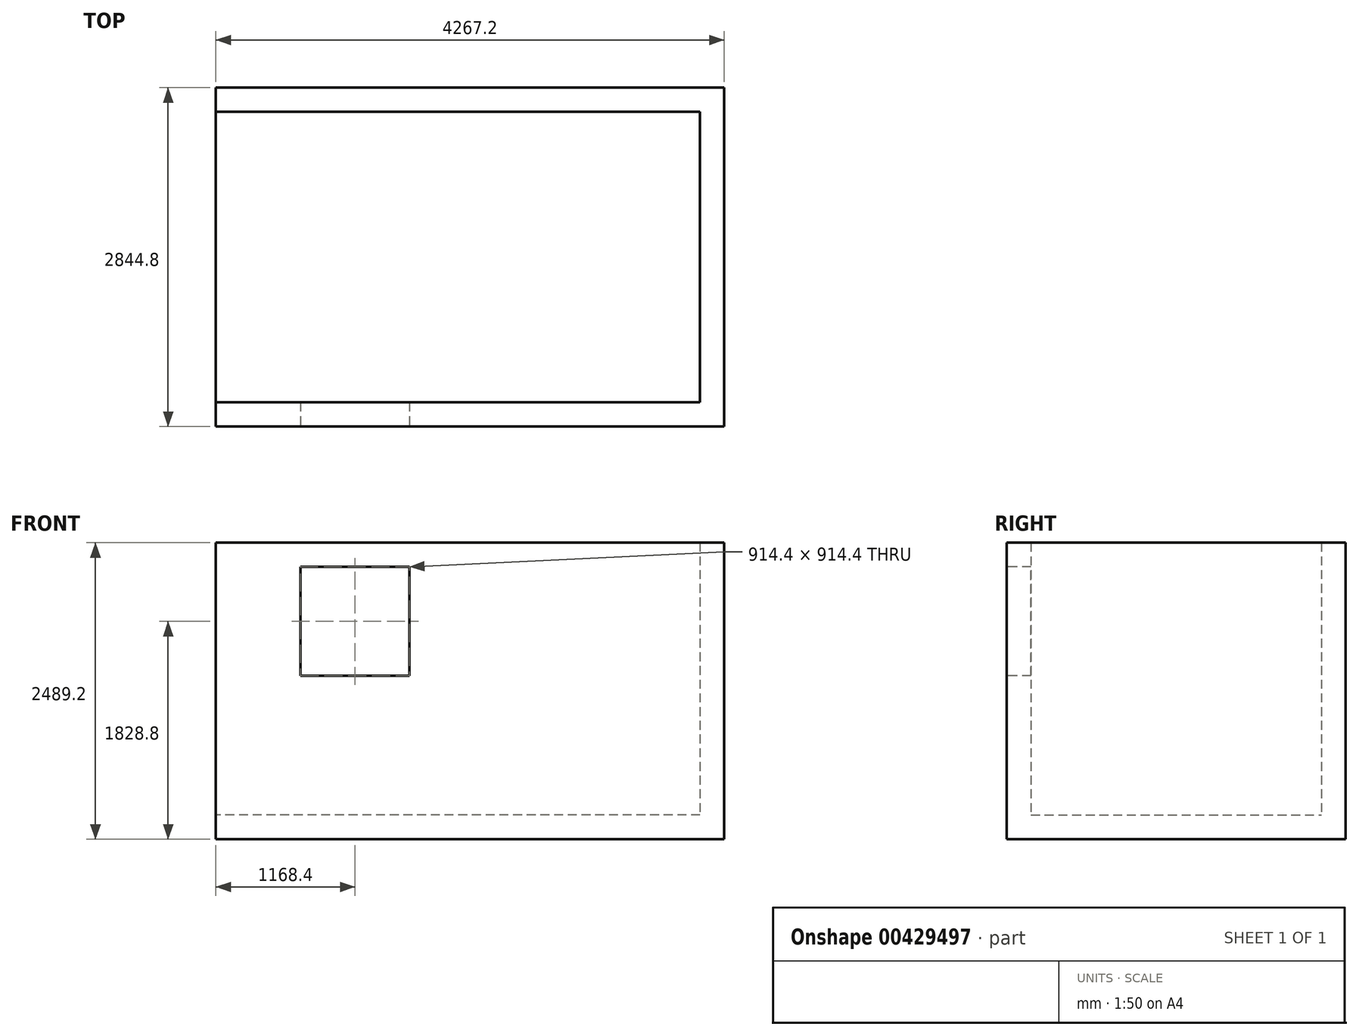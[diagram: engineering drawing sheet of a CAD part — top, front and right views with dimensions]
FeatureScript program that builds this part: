
annotation { "Feature Type Name" : "Feature", "Feature Type Description" : "" }
export const myFeature = defineFeature(function(context is Context, id is Id, definition is map)
    precondition{}
    {
        {
            var Q0;
            Q0=qCreatedBy(makeId("Top.planeOp"),FACE);
            var sketch = newSketch(context, id + "F0", { "sketchPlane" : qUnion([Q0])});
            skLineSegment(sketch, "E0.bottom", {"start": v(0, 0) * mm, "end": v(4267.2, 0) * mm});
            skLineSegment(sketch, "E0.top", {"start": v(0, 2844.8) * mm, "end": v(4267.2, 2844.8) * mm});
            skLineSegment(sketch, "E0.left", {"start": v(0, 0) * mm, "end": v(0, 2844.8) * mm});
            skLineSegment(sketch, "E0.right", {"start": v(4267.2, 0) * mm, "end": v(4267.2, 2844.8) * mm});
            skSolve(sketch);
        }
        {
            var Q0;
            Q0 = qSketchRegion(id + "F0", true);
            extrude(context, id + "F1", {"entities" : qUnion([Q0]), "depth" : 203.2 * mm});
        }
        {
            var Q0;
            Q0=makeQuery(id+"F1.opExtrude","CAP_FACE",FACE,{"disambiguationData":[OSD([sQuery(id+"F0.wireOp",EDGE,"E0.bottom"),sQuery(id+"F0.wireOp",EDGE,"E0.top"),sQuery(id+"F0.wireOp",EDGE,"E0.left"),sQuery(id+"F0.wireOp",EDGE,"E0.right")])],"isStart":false});
            var sketch = newSketch(context, id + "F2", { "sketchPlane" : qUnion([Q0])});
            skLineSegment(sketch, "E1.0", {"start": v(0, 0) * mm, "end": v(4267.2, 0) * mm});
            skLineSegment(sketch, "E1.1", {"start": v(4267.2, 0) * mm, "end": v(4267.2, 2844.8) * mm});
            skLineSegment(sketch, "E1.2", {"start": v(0, 2844.8) * mm, "end": v(4267.2, 2844.8) * mm});
            skLineSegment(sketch, "E2", {"start": v(0, 2844.8) * mm, "end": v(0, 2641.6) * mm});
            skLineSegment(sketch, "E3", {"start": v(0, 2641.6) * mm, "end": v(4064, 2641.6) * mm});
            skLineSegment(sketch, "E4", {"start": v(4064, 2641.6) * mm, "end": v(4064, 203.2) * mm});
            skLineSegment(sketch, "E5", {"start": v(4064, 203.2) * mm, "end": v(0, 203.2) * mm});
            skLineSegment(sketch, "E6", {"start": v(0, 203.2) * mm, "end": v(0, 0) * mm});
            skSolve(sketch);
        }
        {
            var Q0;
            Q0 = qSketchRegion(id + "F2", true);
            extrude(context, id + "F3", {"entities" : qUnion([Q0]), "operationType" : NewBodyOperationType.ADD, "depth" : 2286 * mm});
        }
        {
            var Q0;
            Q0=makeQuery(id+"F3.boolean.opBoolean","MERGE",FACE,{"derivedFrom":[makeQuery(id+"F1.opExtrude","SWEPT_FACE",FACE,{"disambiguationData":[OSD([sQuery(id+"F0.wireOp",EDGE,"E0.bottom")])]}),makeQuery(id+"F3.opExtrude","SWEPT_FACE",FACE,{"disambiguationData":[OSD([sQuery(id+"F2.wireOp",EDGE,"E1.0")])]})]});
            var sketch = newSketch(context, id + "F4", { "sketchPlane" : qUnion([Q0])});
            skLineSegment(sketch, "E7.bottom", {"start": v(711.2, 2286) * mm, "end": v(1625.6, 2286) * mm});
            skLineSegment(sketch, "E7.top", {"start": v(711.2, 1371.6) * mm, "end": v(1625.6, 1371.6) * mm});
            skLineSegment(sketch, "E7.left", {"start": v(711.2, 2286) * mm, "end": v(711.2, 1371.6) * mm});
            skLineSegment(sketch, "E7.right", {"start": v(1625.6, 2286) * mm, "end": v(1625.6, 1371.6) * mm});
            skSolve(sketch);
        }
        {
            var Q0;
            Q0 = qSketchRegion(id + "F4", true);
            var Q1;
            Q1=makeQuery(id+"F3.opExtrude","SWEPT_FACE",FACE,{"disambiguationData":[OSD([sQuery(id+"F2.wireOp",EDGE,"E5")])]});
            extrude(context, id + "F5", {"entities" : qUnion([Q0]), "operationType" : NewBodyOperationType.REMOVE, "endBound" : BoundingType.UP_TO_SURFACE, "oppositeDirection" : true, "endBoundEntityFace" : qUnion([Q1]), "depth" : 25.4 * mm});
        }
    });
